# Revit family: Faucet-Lavatory-KOHLER-ATOM-K-30447T_1
name_source: partatom
category: Plumbing Fixtures
revit_build: Autodesk Revit 2017 (Build: 20160225_1515(x64)
units: mm (PartAtom-declared; Revit-internal decimal feet)

## family parameters
Cut with Voids When Loaded = No
Host = Face
OmniClass Number = 23.31.11.00
OmniClass Title = Faucets
Part Type = Normal
Room Calculation Point = No
Round Connector Dimension = Use Diameter
Shared = No

## types (2) — shared parameters
ADA Compliant = No
Assembly Code = D2010
CW Connection = Yes
Cold Water Inlet = Cold Water Inlet
Date Modified = 08/25/2021
Default Elevation = 36"
Faucet Hole Spacing = 0"
Finish = Kohler-Metal-CP-Polished_Chrome
Flow Rate = 2 GPM
Handle Clearance = 2 15/16"
Height = 5 5/8"
Hot Water Inlet = Hot Water Inlet
Length = 4 5/16"
Manufacturer = KOHLER Co.
Master Format 2014 = 22 41 39
Master Format 2014 Name = Residential Faucets, Supplies, and Trim
Material = Premium Metal Construction
Pressure = 45.00 psi
Product Name = ATOM
Spout Reach = 4 5/16"
URL = https://www.kohlerasiapacific.com
Vent Connection = No
Waste Connection = No
Waste Water Outlet = Waste Water Outlet
WaterSense Certified = No
Width = 2"

## per-type parameters (varying)
| type | 30447T_4 | 30447T_4CD | Description | Drain Included | HW Connection | Hot Water Diameter | Model | Type |
| Mixing Faucet, CP-Polished Chrome | Yes | No | Single Handle Lavatory Faucet Lever Handle, Pop Up | Yes | Yes | 1/2" | K-30447T-4-CP | 1 |
| Cold Only Faucet, CP-Polished Chrome | No | Yes | Single Handle Lavatory Faucet Lever Handle, Cold Only | No | No | 0" | K-30447T-4CD-CP | 2 |

## geometry (parser evidence)
native form markers: Sweep x5
no freeform markers — native parametric forms only
